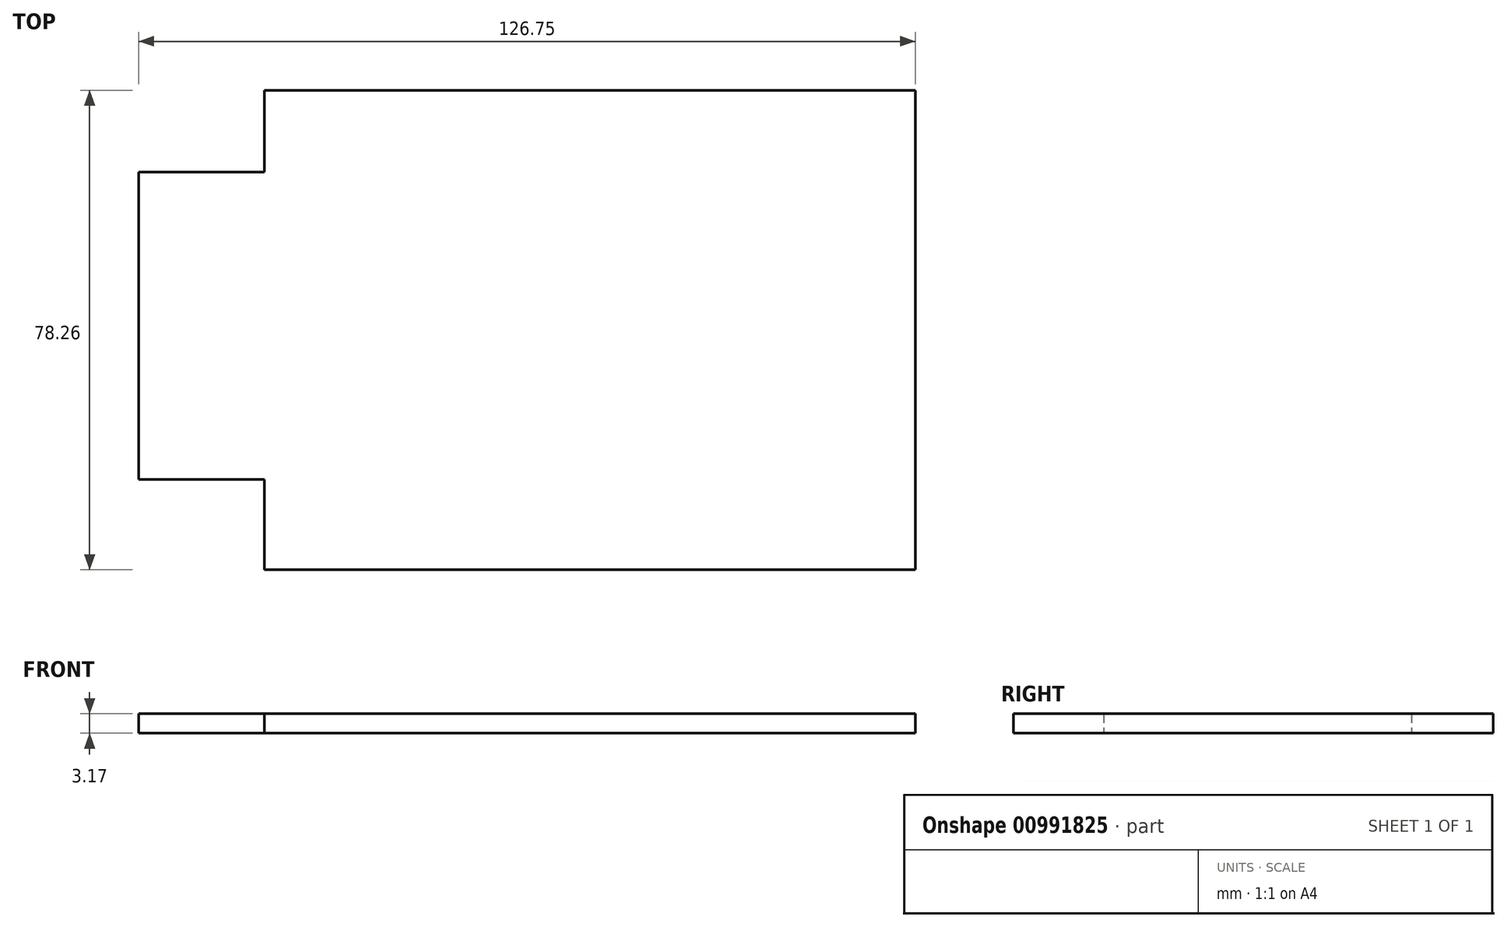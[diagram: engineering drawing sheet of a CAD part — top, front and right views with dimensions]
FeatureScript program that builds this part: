
annotation { "Feature Type Name" : "Feature", "Feature Type Description" : "" }
export const myFeature = defineFeature(function(context is Context, id is Id, definition is map)
    precondition{}
    {
        {
            var Q0;
            Q0=qCreatedBy(makeId("Top.planeOp"),FACE);
            var sketch = newSketch(context, id + "F0", { "sketchPlane" : qUnion([Q0])});
            skLineSegment(sketch, "E0.bottom", {"start": v(-52.8, 62.12) * mm, "end": v(53.42, 62.12) * mm});
            skLineSegment(sketch, "E0.top", {"start": v(-52.8, -16.14) * mm, "end": v(53.42, -16.14) * mm});
            skLineSegment(sketch, "E0.left", {"start": v(-52.8, 62.12) * mm, "end": v(-52.8, -16.14) * mm});
            skLineSegment(sketch, "E0.right", {"start": v(53.42, 62.12) * mm, "end": v(53.42, -16.14) * mm});
            skLineSegment(sketch, "E1.left", {"start": v(-52.8, 57.5) * mm, "end": v(-52.8, 7.3) * mm});
            skLineSegment(sketch, "E2.bottom", {"start": v(-52.8, 48.8) * mm, "end": v(-73.33, 48.8) * mm});
            skLineSegment(sketch, "E2.top", {"start": v(-52.8, -1.4) * mm, "end": v(-73.33, -1.4) * mm});
            skLineSegment(sketch, "E2.left", {"start": v(-52.8, 48.8) * mm, "end": v(-52.8, -1.4) * mm});
            skLineSegment(sketch, "E2.right", {"start": v(-73.33, 48.8) * mm, "end": v(-73.33, -1.4) * mm});
            skSolve(sketch);
        }
        {
            var Q0;
            {var subQ4=sQuery(id+"F0.wireOp",EDGE,"E0.bottom");Q0=makeQuery(id+"F0.imprint","IMPRINT",FACE,{"disambiguationData":[TD([[makeQuery(id+"F0.imprint","IMPRINT",EDGE,{"derivedFrom":subQ4}),-1.0]])]});}
            var Q1;
            {var subQ3=sQuery(id+"F0.wireOp",EDGE,"E2.bottom");Q1=makeQuery(id+"F0.imprint","IMPRINT",FACE,{"disambiguationData":[TD([[makeQuery(id+"F0.imprint","IMPRINT",EDGE,{"derivedFrom":subQ3}),1.0]])]});}
            extrude(context, id + "F1", {"entities" : qUnion([Q0, Q1]), "depth" : 3.17 * mm, "offsetDistance" : 25.4 * mm});
        }
    });
